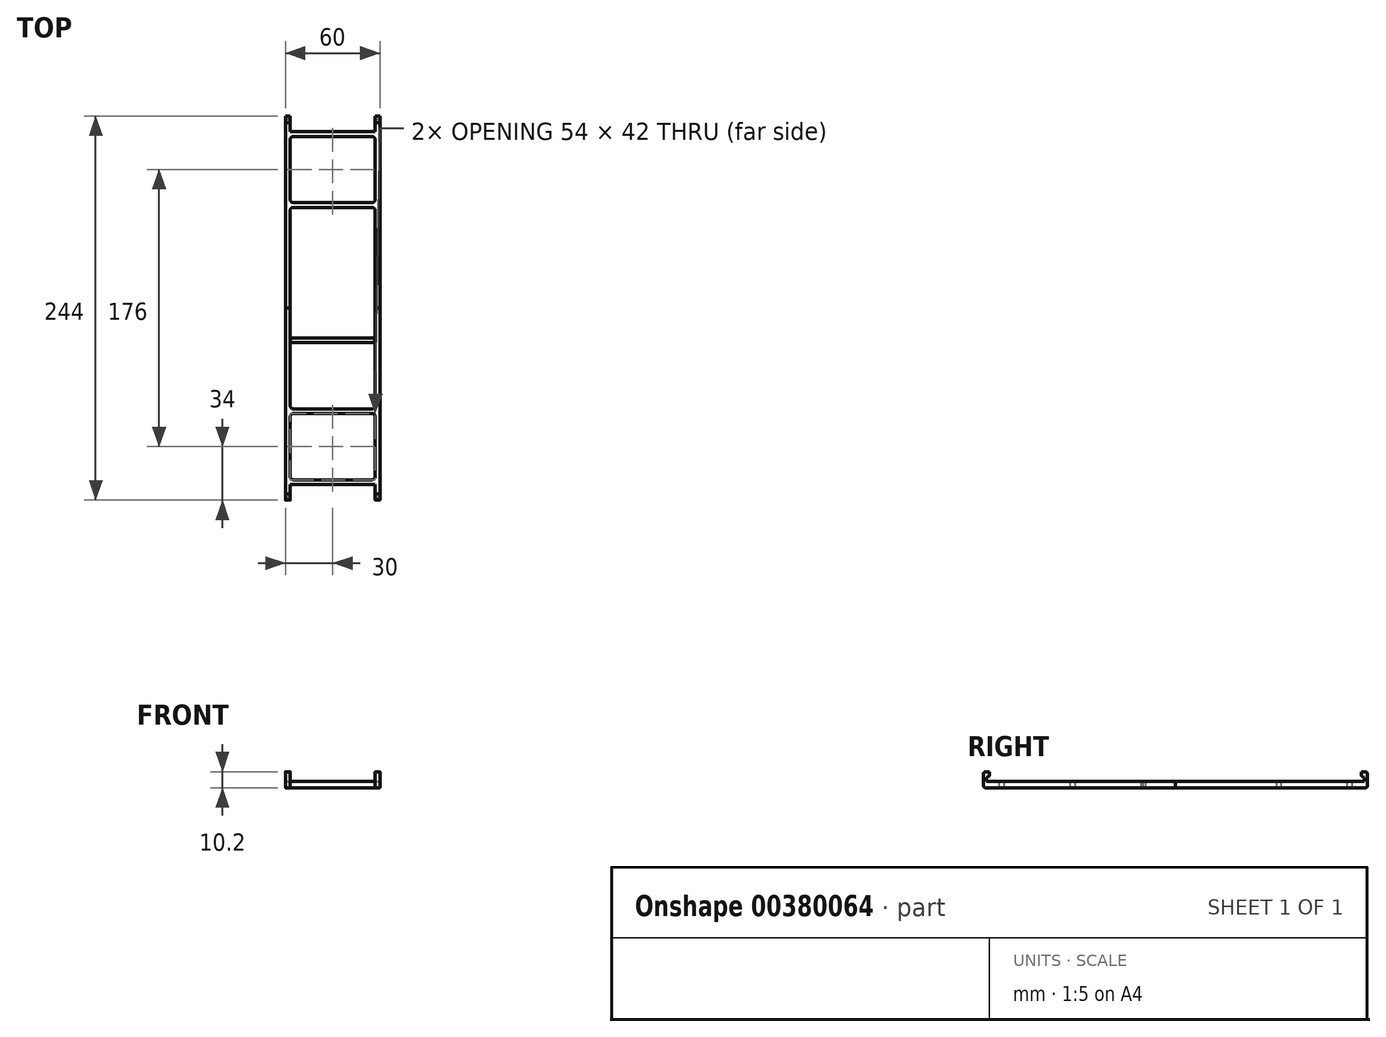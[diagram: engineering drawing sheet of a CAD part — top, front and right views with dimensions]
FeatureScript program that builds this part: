
annotation { "Feature Type Name" : "Feature", "Feature Type Description" : "" }
export const myFeature = defineFeature(function(context is Context, id is Id, definition is map)
    precondition{}
    {
        {
            var Q0;
            Q0=qCreatedBy(makeId("Front.planeOp"),FACE);
            var sketch = newSketch(context, id + "F0", { "sketchPlane" : qUnion([Q0])});
            skLineSegment(sketch, "E0.bottom", {"start": v(-31.5, 4) * mm, "end": v(-28.5, 4) * mm});
            skLineSegment(sketch, "E0.top", {"start": v(-31.5, 0) * mm, "end": v(-28.5, 0) * mm});
            skLineSegment(sketch, "E0.left", {"start": v(-31.5, 4) * mm, "end": v(-31.5, 0) * mm});
            skLineSegment(sketch, "E0.right", {"start": v(-28.5, 4) * mm, "end": v(-28.5, 0) * mm});
            skLineSegment(sketch, "E1.bottom", {"start": v(25.5, 4) * mm, "end": v(28.5, 4) * mm});
            skLineSegment(sketch, "E1.top", {"start": v(25.5, 0) * mm, "end": v(28.5, 0) * mm});
            skLineSegment(sketch, "E1.left", {"start": v(28.5, 4) * mm, "end": v(28.5, 0) * mm});
            skLineSegment(sketch, "E1.right", {"start": v(25.5, 4) * mm, "end": v(25.5, 0) * mm});
            skSolve(sketch);
        }
        {
            var Q0;
            Q0 = qSketchRegion(id + "F0", true);
            extrude(context, id + "F1", {"entities" : qUnion([Q0]), "depth" : 122 * mm});
        }
        {
            var Q0;
            Q0=makeQuery(id+"F1.opExtrude","SWEPT_FACE",FACE,{"disambiguationData":[OSD([sQuery(id+"F0.wireOp",EDGE,"E0.right")])]});
            var sketch = newSketch(context, id + "F2", { "sketchPlane" : qUnion([Q0])});
            skLineSegment(sketch, "E2.bottom", {"start": v(-112, 4) * mm, "end": v(-109, 4) * mm});
            skLineSegment(sketch, "E2.top", {"start": v(-112, 0) * mm, "end": v(-109, 0) * mm});
            skLineSegment(sketch, "E2.left", {"start": v(-112, 4) * mm, "end": v(-112, 0) * mm});
            skLineSegment(sketch, "E2.right", {"start": v(-109, 4) * mm, "end": v(-109, 0) * mm});
            skLineSegment(sketch, "E3.1.0.0", {"start": v(-67, 4) * mm, "end": v(-64, 4) * mm});
            skLineSegment(sketch, "E3.1.0.1", {"start": v(-64, 4) * mm, "end": v(-64, 0) * mm});
            skLineSegment(sketch, "E3.1.0.2", {"start": v(-67, 0) * mm, "end": v(-64, 0) * mm});
            skLineSegment(sketch, "E3.1.0.3", {"start": v(-67, 4) * mm, "end": v(-67, 0) * mm});
            skLineSegment(sketch, "E3.direction1", {"start": v(-112, 4) * mm, "end": v(-67, 4) * mm, "construction": true});
            skLineSegment(sketch, "E4.0.2.0", {"start": v(-22, 4) * mm, "end": v(-19, 4) * mm});
            skLineSegment(sketch, "E4.3.2.0", {"start": v(-19, 4) * mm, "end": v(-19, 0) * mm});
            skLineSegment(sketch, "E4.6.2.0", {"start": v(-22, 0) * mm, "end": v(-19, 0) * mm});
            skLineSegment(sketch, "E4.9.2.0", {"start": v(-22, 4) * mm, "end": v(-22, 0) * mm});
            skSolve(sketch);
        }
        {
            var Q0;
            Q0 = qSketchRegion(id + "F2", true);
            extrude(context, id + "F3", {"entities" : qUnion([Q0]), "endBound" : BoundingType.UP_TO_NEXT, "depth" : 25 * mm});
        }
        {
            var Q0;
            Q0=makeQuery(id+"F1.opExtrude","SWEPT_BODY",BODY,{"disambiguationData":[OSD([sQuery(id+"F0.wireOp",EDGE,"E0.bottom"),sQuery(id+"F0.wireOp",EDGE,"E0.top"),sQuery(id+"F0.wireOp",EDGE,"E0.left"),sQuery(id+"F0.wireOp",EDGE,"E0.right")])]});
            var Q1;
            Q1=makeQuery(id+"F1.opExtrude","SWEPT_BODY",BODY,{"disambiguationData":[OSD([sQuery(id+"F0.wireOp",EDGE,"E1.bottom"),sQuery(id+"F0.wireOp",EDGE,"E1.top"),sQuery(id+"F0.wireOp",EDGE,"E1.left"),sQuery(id+"F0.wireOp",EDGE,"E1.right")])]});
            var Q2;
            Q2=makeQuery(id+"F3.opExtrude","SWEPT_BODY",BODY,{"disambiguationData":[OSD([sQuery(id+"F2.wireOp",EDGE,"E2.bottom"),sQuery(id+"F2.wireOp",EDGE,"E2.top"),sQuery(id+"F2.wireOp",EDGE,"E2.left"),sQuery(id+"F2.wireOp",EDGE,"E2.right")])]});
            var Q3;
            Q3=makeQuery(id+"F3.opExtrude","SWEPT_BODY",BODY,{"disambiguationData":[OSD([sQuery(id+"F2.wireOp",EDGE,"E3.1.0.0"),sQuery(id+"F2.wireOp",EDGE,"E3.1.0.1"),sQuery(id+"F2.wireOp",EDGE,"E3.1.0.2"),sQuery(id+"F2.wireOp",EDGE,"E3.1.0.3")])]});
            var Q4;
            Q4=makeQuery(id+"F3.opExtrude","SWEPT_BODY",BODY,{"disambiguationData":[OSD([sQuery(id+"F2.wireOp",EDGE,"E3.2.0.0"),sQuery(id+"F2.wireOp",EDGE,"E3.2.0.1"),sQuery(id+"F2.wireOp",EDGE,"E3.2.0.2"),sQuery(id+"F2.wireOp",EDGE,"E3.2.0.3")])]});
            var Q5;
            Q5=makeQuery(id+"F3.opExtrude","SWEPT_BODY",BODY,{"disambiguationData":[OSD([sQuery(id+"F2.wireOp",EDGE,"E3.3.0.0"),sQuery(id+"F2.wireOp",EDGE,"E3.3.0.1"),sQuery(id+"F2.wireOp",EDGE,"E3.3.0.2"),sQuery(id+"F2.wireOp",EDGE,"E3.3.0.3")])]});
            var Q6;
            Q6=makeQuery(id+"F3.opExtrude","SWEPT_BODY",BODY,{"disambiguationData":[OSD([sQuery(id+"F2.wireOp",EDGE,"ef4f69a2-6a8d-410e-8b05-ba4ff120e582.0.4.0"),sQuery(id+"F2.wireOp",EDGE,"ef4f69a2-6a8d-410e-8b05-ba4ff120e582.3.4.0"),sQuery(id+"F2.wireOp",EDGE,"ef4f69a2-6a8d-410e-8b05-ba4ff120e582.6.4.0"),sQuery(id+"F2.wireOp",EDGE,"ef4f69a2-6a8d-410e-8b05-ba4ff120e582.9.4.0")])]});
            booleanBodies(context, id + "F4", {"operationType" : BooleanOperationType.UNION, "tools" : qUnion([Q0, Q1, Q2, Q3, Q4, Q5, Q6])});
        }
        {
            var Q0;
            {var subQ1=sQuery(id+"F0.wireOp",EDGE,"E0.right");Q0=makeQuery(id+"F4.opBoolean","SPLIT",FACE,{"disambiguationData":[TD([makeQuery(id+"F3.opExtrude","SWEPT_FACE",FACE,{"disambiguationData":[OSD([sQuery(id+"F2.wireOp",EDGE,"E2.left")])]})])],"derivedFrom":makeQuery(id+"F1.opExtrude","SWEPT_FACE",FACE,{"disambiguationData":[OSD([subQ1])]})});}
            var sketch = newSketch(context, id + "F5", { "sketchPlane" : qUnion([Q0])});
            skLineSegment(sketch, "E5.bottom", {"start": v(-122, 4) * mm, "end": v(-120, 4) * mm});
            skLineSegment(sketch, "E5.left", {"start": v(-122, 4) * mm, "end": v(-122, 7.2) * mm});
            skLineSegment(sketch, "E5.right", {"start": v(-120, 4) * mm, "end": v(-120, 7.2) * mm});
            skLineSegment(sketch, "E6.bottom", {"start": v(-120, 7.2) * mm, "end": v(-118, 7.2) * mm});
            skLineSegment(sketch, "E6.top", {"start": v(-122, 10.2) * mm, "end": v(-118, 10.2) * mm});
            skLineSegment(sketch, "E6.left", {"start": v(-122, 7.2) * mm, "end": v(-122, 10.2) * mm});
            skLineSegment(sketch, "E6.right", {"start": v(-118, 7.2) * mm, "end": v(-118, 10.2) * mm});
            skSolve(sketch);
        }
        {
            var Q0;
            Q0=makeQuery(id+"F5.imprint","IMPRINT",FACE,{"disambiguationData":[TD([[makeQuery(id+"F5.imprint","IMPRINT",EDGE,{"derivedFrom":sQuery(id+"F5.wireOp",EDGE,"E5.bottom")}),1.0]])]});
            var Q1;
            Q1=makeQuery(id+"F1.opExtrude","SWEPT_FACE",FACE,{"disambiguationData":[OSD([sQuery(id+"F0.wireOp",EDGE,"E0.left")])]});
            extrude(context, id + "F6", {"entities" : qUnion([Q0]), "operationType" : NewBodyOperationType.ADD, "endBound" : BoundingType.UP_TO_SURFACE, "oppositeDirection" : true, "endBoundEntityFace" : qUnion([Q1]), "depth" : 25 * mm});
        }
        {
            var Q0;
            Q0=makeQuery(id+"F1.opExtrude","SWEPT_FACE",FACE,{"disambiguationData":[OSD([sQuery(id+"F0.wireOp",EDGE,"E1.left")])]});
            var sketch = newSketch(context, id + "F7", { "sketchPlane" : qUnion([Q0])});
            skLineSegment(sketch, "E7.bottom", {"start": v(-122, 4) * mm, "end": v(-120, 4) * mm});
            skLineSegment(sketch, "E7.left", {"start": v(-122, 4) * mm, "end": v(-122, 7.2) * mm});
            skLineSegment(sketch, "E7.right", {"start": v(-120, 4) * mm, "end": v(-120, 7.2) * mm});
            skLineSegment(sketch, "E8.bottom", {"start": v(-120, 7.2) * mm, "end": v(-118, 7.2) * mm});
            skLineSegment(sketch, "E8.top", {"start": v(-122, 10.2) * mm, "end": v(-118, 10.2) * mm});
            skLineSegment(sketch, "E8.left", {"start": v(-122, 7.2) * mm, "end": v(-122, 10.2) * mm});
            skLineSegment(sketch, "E8.right", {"start": v(-118, 7.2) * mm, "end": v(-118, 10.2) * mm});
            skSolve(sketch);
        }
        {
            var Q0;
            Q0=makeQuery(id+"F7.imprint","IMPRINT",FACE,{"disambiguationData":[TD([[makeQuery(id+"F7.imprint","IMPRINT",EDGE,{"derivedFrom":sQuery(id+"F7.wireOp",EDGE,"E7.bottom")}),1.0]])]});
            var Q1;
            {var subQ1=sQuery(id+"F0.wireOp",EDGE,"E1.right");Q1=makeQuery(id+"F4.opBoolean","SPLIT",FACE,{"disambiguationData":[TD([makeQuery(id+"F3.opExtrude","SWEPT_FACE",FACE,{"disambiguationData":[OSD([sQuery(id+"F2.wireOp",EDGE,"E2.left")])]})])],"derivedFrom":makeQuery(id+"F1.opExtrude","SWEPT_FACE",FACE,{"disambiguationData":[OSD([subQ1])]})});}
            extrude(context, id + "F8", {"entities" : qUnion([Q0]), "operationType" : NewBodyOperationType.ADD, "endBound" : BoundingType.UP_TO_SURFACE, "oppositeDirection" : true, "endBoundEntityFace" : qUnion([Q1]), "depth" : 25 * mm});
        }
        {
            var Q0;
            Q0=makeQuery(id+"F1.opExtrude","CAP_EDGE",EDGE,{"disambiguationData":[OSD([sQuery(id+"F0.wireOp",EDGE,"E0.top")])],"isStart":false});
            var Q1;
            Q1=makeQuery(id+"F1.opExtrude","CAP_EDGE",EDGE,{"disambiguationData":[OSD([sQuery(id+"F0.wireOp",EDGE,"E1.top")])],"isStart":false});
            var Q2;
            Q2=makeQuery(id+"F8.opExtrude","SWEPT_EDGE",EDGE,{"disambiguationData":[OSD([sQuery(id+"F7.wireOp",EDGE,"E8.top"),sQuery(id+"F7.wireOp",EDGE,"E8.left")])]});
            var Q3;
            Q3=makeQuery(id+"F6.opExtrude","SWEPT_EDGE",EDGE,{"disambiguationData":[OSD([sQuery(id+"F5.wireOp",EDGE,"E6.top"),sQuery(id+"F5.wireOp",EDGE,"E6.left")])]});
            var Q4;
            Q4=makeQuery(id+"F8.opExtrude","SWEPT_EDGE",EDGE,{"disambiguationData":[OSD([sQuery(id+"F0.wireOp",EDGE,"E1.bottom"),sQuery(id+"F0.wireOp",EDGE,"E1.left"),sQuery(id+"F7.wireOp",EDGE,"E7.bottom"),sQuery(id+"F7.wireOp",EDGE,"E7.right")])]});
            var Q5;
            Q5=makeQuery(id+"F8.opExtrude","SWEPT_EDGE",EDGE,{"disambiguationData":[OSD([sQuery(id+"F7.wireOp",EDGE,"E7.right"),sQuery(id+"F7.wireOp",EDGE,"E8.bottom")])]});
            var Q6;
            Q6=makeQuery(id+"F6.opExtrude","SWEPT_EDGE",EDGE,{"disambiguationData":[OSD([sQuery(id+"F0.wireOp",EDGE,"E0.bottom"),sQuery(id+"F0.wireOp",EDGE,"E0.right"),sQuery(id+"F5.wireOp",EDGE,"E5.bottom"),sQuery(id+"F5.wireOp",EDGE,"E5.right")])]});
            var Q7;
            Q7=makeQuery(id+"F6.opExtrude","SWEPT_EDGE",EDGE,{"disambiguationData":[OSD([sQuery(id+"F5.wireOp",EDGE,"E5.right"),sQuery(id+"F5.wireOp",EDGE,"E6.bottom")])]});
            fillet(context, id + "F9", {"entities" : qUnion([Q0, Q1, Q2, Q3, Q4, Q5, Q6, Q7]), "radius" : 1.5 * mm, "tangentPropagation" : true, "allowEdgeOverflow" : false});
        }
        {
            var Q0;
            Q0=makeQuery(id+"F6.opExtrude","SWEPT_EDGE",EDGE,{"disambiguationData":[OSD([sQuery(id+"F5.wireOp",EDGE,"E6.bottom"),sQuery(id+"F5.wireOp",EDGE,"E6.right")])]});
            var Q1;
            Q1=makeQuery(id+"F8.opExtrude","SWEPT_EDGE",EDGE,{"disambiguationData":[OSD([sQuery(id+"F7.wireOp",EDGE,"E8.bottom"),sQuery(id+"F7.wireOp",EDGE,"E8.right")])]});
            fillet(context, id + "F10", {"entities" : qUnion([Q0, Q1]), "radius" : 1 * mm, "tangentPropagation" : true, "allowEdgeOverflow" : false});
        }
        {
            var Q0;
            Q0=makeQuery(id+"F3.opExtrude","CAP_EDGE",EDGE,{"disambiguationData":[OSD([sQuery(id+"F2.wireOp",EDGE,"E2.right")])],"isStart":true});
            var Q1;
            Q1=makeQuery(id+"F3.opExtrude","CAP_EDGE",EDGE,{"disambiguationData":[OSD([sQuery(id+"F2.wireOp",EDGE,"E3.1.0.1")])],"isStart":true});
            var Q2;
            Q2=makeQuery(id+"F3.opExtrude","CAP_EDGE",EDGE,{"disambiguationData":[OSD([sQuery(id+"F2.wireOp",EDGE,"E2.right")])],"isStart":false});
            var Q3;
            Q3=makeQuery(id+"F3.opExtrude","CAP_EDGE",EDGE,{"disambiguationData":[OSD([sQuery(id+"F2.wireOp",EDGE,"E4.9.2.0")])],"isStart":false});
            var Q4;
            Q4=makeQuery(id+"F3.opExtrude","CAP_EDGE",EDGE,{"disambiguationData":[OSD([sQuery(id+"F2.wireOp",EDGE,"E3.1.0.3")])],"isStart":false});
            var Q5;
            Q5=makeQuery(id+"F3.opExtrude","CAP_EDGE",EDGE,{"disambiguationData":[OSD([sQuery(id+"F2.wireOp",EDGE,"E3.1.0.3")])],"isStart":true});
            var Q6;
            Q6=makeQuery(id+"F3.opExtrude","CAP_EDGE",EDGE,{"disambiguationData":[OSD([sQuery(id+"F2.wireOp",EDGE,"E4.9.2.0")])],"isStart":true});
            var Q7;
            Q7=makeQuery(id+"F3.opExtrude","CAP_EDGE",EDGE,{"disambiguationData":[OSD([sQuery(id+"F2.wireOp",EDGE,"E4.3.2.0")])],"isStart":true});
            var Q8;
            Q8=makeQuery(id+"F3.opExtrude","CAP_EDGE",EDGE,{"disambiguationData":[OSD([sQuery(id+"F2.wireOp",EDGE,"E2.left")])],"isStart":true});
            var Q9;
            Q9=makeQuery(id+"F3.opExtrude","CAP_EDGE",EDGE,{"disambiguationData":[OSD([sQuery(id+"F2.wireOp",EDGE,"E2.left")])],"isStart":false});
            var Q10;
            Q10=makeQuery(id+"F3.opExtrude","CAP_EDGE",EDGE,{"disambiguationData":[OSD([sQuery(id+"F2.wireOp",EDGE,"E3.1.0.1")])],"isStart":false});
            var Q11;
            Q11=makeQuery(id+"F3.opExtrude","CAP_EDGE",EDGE,{"disambiguationData":[OSD([sQuery(id+"F2.wireOp",EDGE,"E4.3.2.0")])],"isStart":false});
            fillet(context, id + "F11", {"entities" : qUnion([Q0, Q1, Q2, Q3, Q4, Q5, Q6, Q7, Q8, Q9, Q10, Q11]), "radius" : 2 * mm, "tangentPropagation" : true, "allowEdgeOverflow" : false});
        }
        {
            var Q0;
            Q0=makeQuery(id+"F1.opExtrude","SWEPT_BODY",BODY,{"disambiguationData":[OSD([sQuery(id+"F0.wireOp",EDGE,"E0.bottom"),sQuery(id+"F0.wireOp",EDGE,"E0.top"),sQuery(id+"F0.wireOp",EDGE,"E0.left"),sQuery(id+"F0.wireOp",EDGE,"E0.right")])]});
            var Q1;
            Q1=qCreatedBy(makeId("Front.planeOp"),FACE);
            mirror(context, id + "F12", {"operationType" : NewBodyOperationType.ADD, "entities" : qUnion([Q0]), "mirrorPlane" : qUnion([Q1])});
        }
    });
